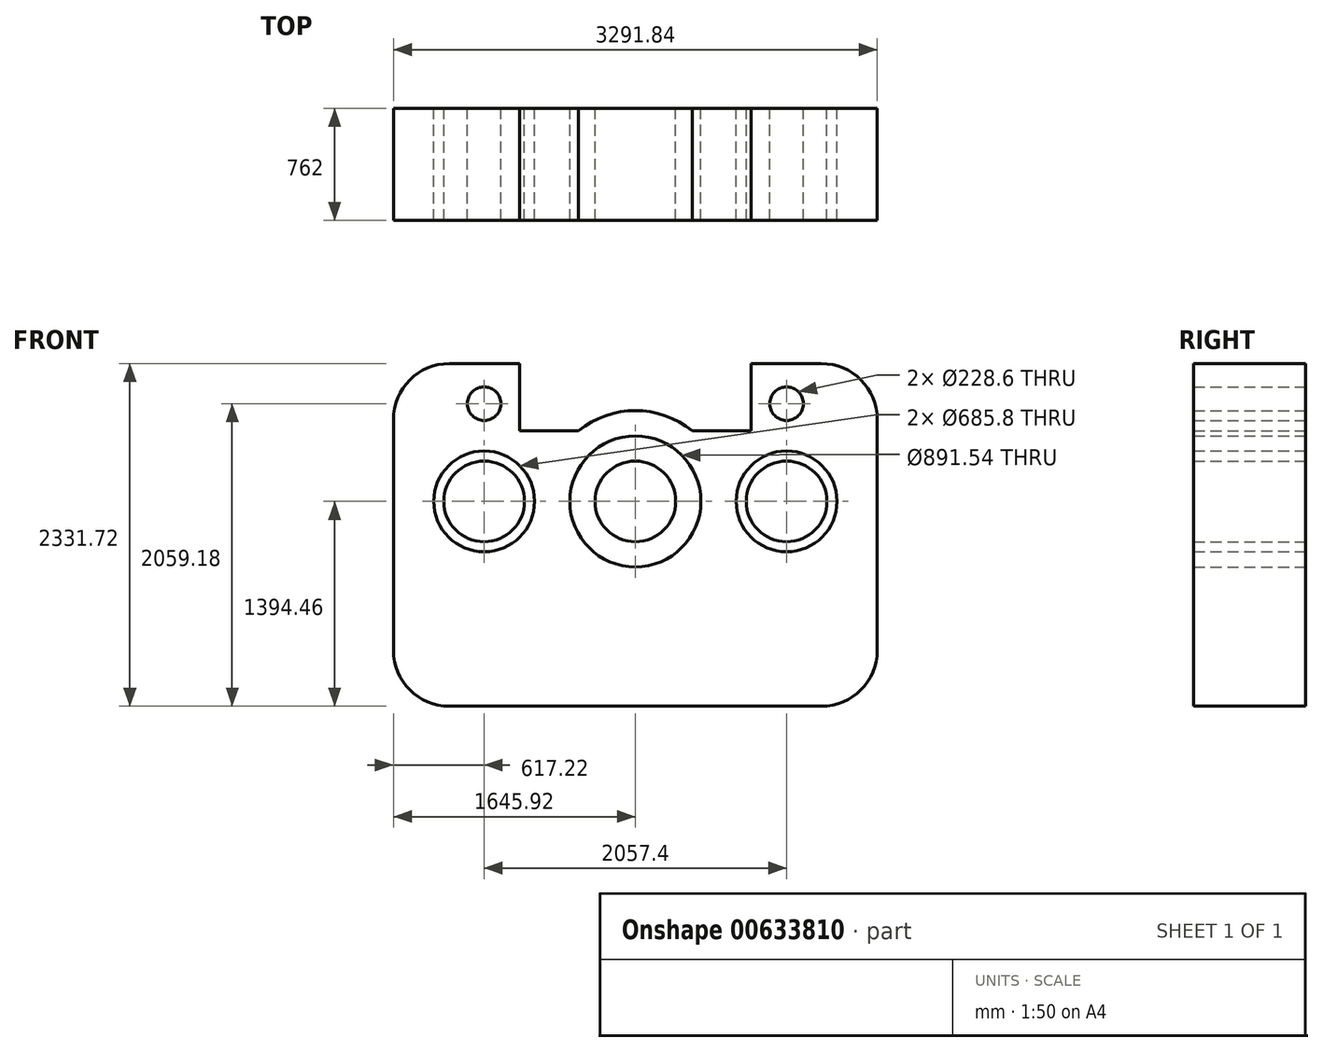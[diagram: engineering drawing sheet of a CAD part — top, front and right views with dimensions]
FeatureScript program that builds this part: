
annotation { "Feature Type Name" : "Feature", "Feature Type Description" : "" }
export const myFeature = defineFeature(function(context is Context, id is Id, definition is map)
    precondition{}
    {
        {
            var Q0;
            Q0=qCreatedBy(makeId("Front.planeOp"),FACE);
            var sketch = newSketch(context, id + "F0", { "sketchPlane" : qUnion([Q0])});
            skLineSegment(sketch, "E0", {"start": v(0, 0) * mm, "end": v(-1264.92, 0) * mm});
            skLineSegment(sketch, "E1", {"start": v(-1645.92, 381) * mm, "end": v(-1645.92, 1950.72) * mm});
            skLineSegment(sketch, "E2", {"start": v(-1264.92, 2331.72) * mm, "end": v(-788.67, 2331.72) * mm});
            skLineSegment(sketch, "E3", {"start": v(1645.92, 1950.72) * mm, "end": v(1645.92, 381) * mm});
            skLineSegment(sketch, "E4", {"start": v(1264.92, 0) * mm, "end": v(0, 0) * mm});
            skLineSegment(sketch, "E5", {"start": v(1264.92, 2331.72) * mm, "end": v(788.67, 2331.72) * mm});
            skLineSegment(sketch, "E6.trimOffspring", {"start": v(788.67, 2331.72) * mm, "end": v(1264.92, 2331.72) * mm});
            skLineSegment(sketch, "E7", {"start": v(-788.67, 2331.72) * mm, "end": v(-786.68, 1874.52) * mm});
            skLineSegment(sketch, "E8", {"start": v(788.67, 2331.72) * mm, "end": v(788.67, 1874.52) * mm});
            skLineSegment(sketch, "E9", {"start": v(788.67, 1874.52) * mm, "end": v(387.95, 1874.52) * mm});
            skCircle(sketch, "E10", {"center": v(-1028.7, 1394.46) * mm, "radius": 274.32 * mm});
            skCircle(sketch, "E11", {"center": v(1028.7, 1394.46) * mm, "radius": 274.32 * mm});
            skCircle(sketch, "E12", {"center": v(-1028.7, 1394.46) * mm, "radius": 342.9 * mm});
            skCircle(sketch, "E13", {"center": v(1028.7, 1394.46) * mm, "radius": 342.9 * mm});
            skCircle(sketch, "E14", {"center": v(0, 1394.46) * mm, "radius": 274.32 * mm});
            skCircle(sketch, "E15", {"center": v(0, 1394.46) * mm, "radius": 445.77 * mm});
            skArc(sketch, "E16", {"start": v(387.95, 1874.52) * mm, "mid": v(0, 2011.68) * mm, "end": v(-387.94, 1874.52) * mm});
            skCircle(sketch, "E17", {"center": v(-1028.7, 2059.18) * mm, "radius": 114.3 * mm});
            skCircle(sketch, "E18", {"center": v(1028.7, 2059.18) * mm, "radius": 114.3 * mm});
            skLineSegment(sketch, "E19.trimOffspring", {"start": v(-387.94, 1874.52) * mm, "end": v(-786.68, 1874.52) * mm});
            skPoint(sketch, "E20.start.orphan", {"position": v(0, 2394.65) * mm});
            skPoint(sketch, "E21.visualSharp", {"position": v(-1645.92, 2331.72) * mm});
            skArc(sketch, "E21.filletArc", {"start": v(-1264.92, 2331.72) * mm, "mid": v(-1534.33, 2220.13) * mm, "end": v(-1645.92, 1950.72) * mm});
            skPoint(sketch, "E22.visualSharp", {"position": v(-1645.92, 0) * mm});
            skArc(sketch, "E22.filletArc", {"start": v(-1645.92, 381) * mm, "mid": v(-1534.33, 111.6) * mm, "end": v(-1264.92, 0) * mm});
            skPoint(sketch, "E23.visualSharp", {"position": v(1645.92, 0) * mm});
            skArc(sketch, "E23.filletArc", {"start": v(1264.92, 0) * mm, "mid": v(1534.33, 111.6) * mm, "end": v(1645.92, 381) * mm});
            skPoint(sketch, "E24.visualSharp", {"position": v(1645.92, 2331.72) * mm});
            skArc(sketch, "E24.filletArc", {"start": v(1645.92, 1950.72) * mm, "mid": v(1534.33, 2220.13) * mm, "end": v(1264.92, 2331.72) * mm});
            skSolve(sketch);
        }
        {
            var Q0;
            Q0 = qSketchRegion(id + "F0", true);
            var Q1;
            Q1=makeQuery(id+"F0.imprint","IMPRINT",FACE,{"disambiguationData":[TD([[makeQuery(id+"F0.imprint","IMPRINT",EDGE,{"derivedFrom":sQuery(id+"F0.wireOp",EDGE,"E10")}),1.0]])]});
            var Q2;
            Q2=makeQuery(id+"F0.imprint","IMPRINT",FACE,{"disambiguationData":[TD([[makeQuery(id+"F0.imprint","IMPRINT",EDGE,{"derivedFrom":sQuery(id+"F0.wireOp",EDGE,"E14")}),1.0]])]});
            var Q3;
            Q3=makeQuery(id+"F0.imprint","IMPRINT",FACE,{"disambiguationData":[TD([[makeQuery(id+"F0.imprint","IMPRINT",EDGE,{"derivedFrom":sQuery(id+"F0.wireOp",EDGE,"E11")}),1.0]])]});
            extrude(context, id + "F1", {"entities" : qUnion([Q0, Q1, Q2, Q3]), "depth" : 762 * mm, "offsetDistance" : 25.4 * mm, "symmetric" : true});
        }
    });
